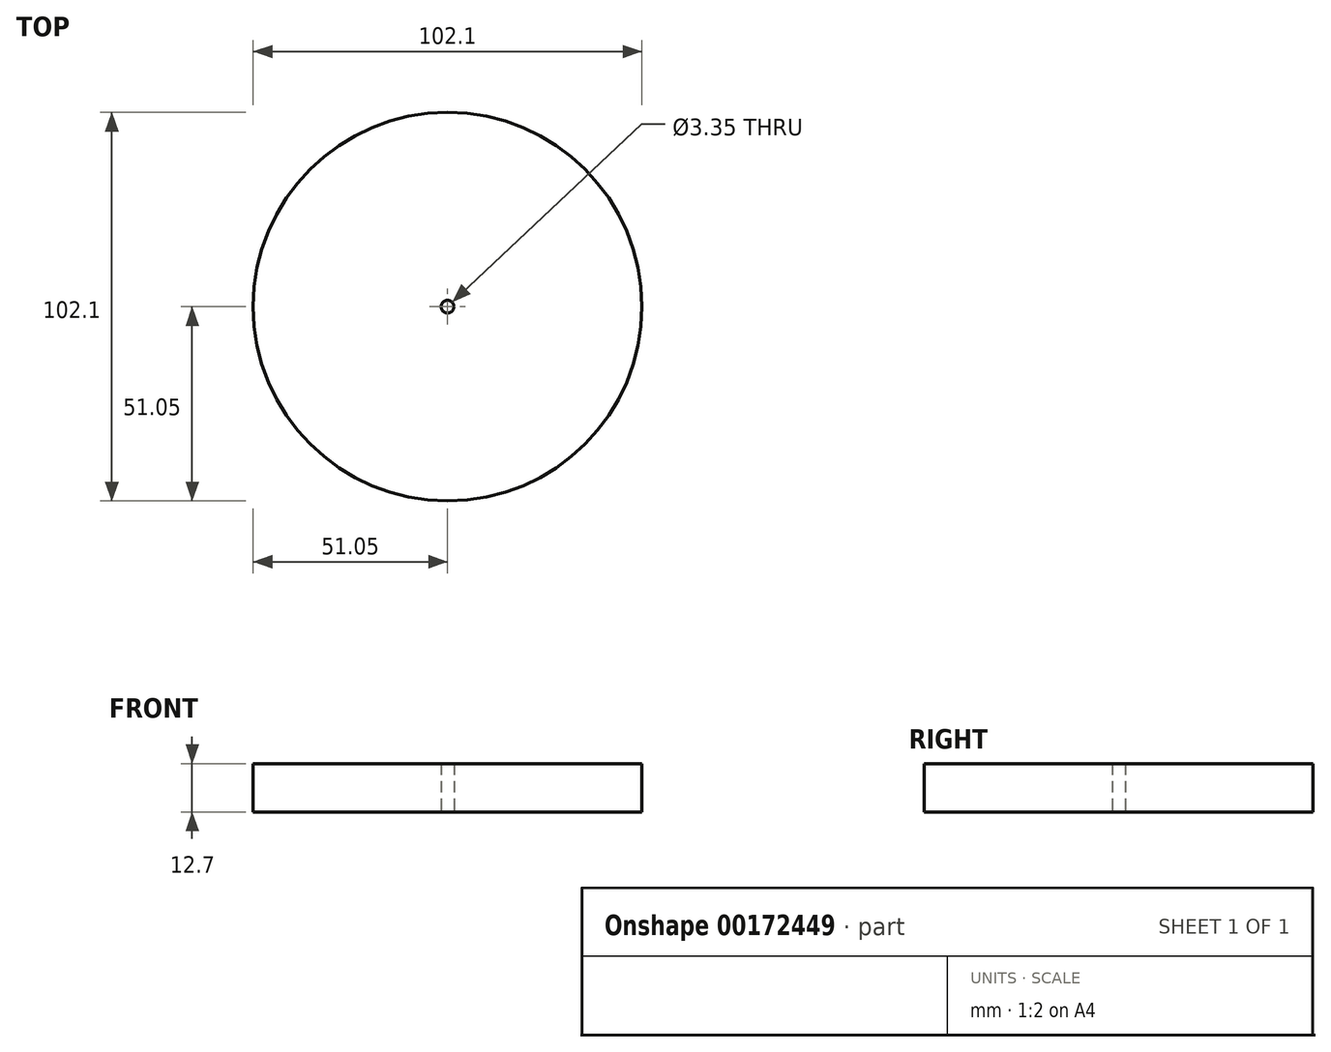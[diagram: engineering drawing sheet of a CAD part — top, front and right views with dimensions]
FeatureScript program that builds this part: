
annotation { "Feature Type Name" : "Feature", "Feature Type Description" : "" }
export const myFeature = defineFeature(function(context is Context, id is Id, definition is map)
    precondition{}
    {
        {
            var Q0;
            Q0=qCreatedBy(makeId("Top.planeOp"),FACE);
            var sketch = newSketch(context, id + "F0", { "sketchPlane" : qUnion([Q0])});
            skCircle(sketch, "E0", {"center": v(0, 0) * mm, "radius": 51.05 * mm});
            skCircle(sketch, "E1", {"center": v(0, 0) * mm, "radius": 22.35 * mm});
            skCircle(sketch, "E2", {"center": v(0, 0) * mm, "radius": 11.28 * mm});
            skCircle(sketch, "E3", {"center": v(0, 0) * mm, "radius": 8.6 * mm});
            skCircle(sketch, "E4", {"center": v(0, 0) * mm, "radius": 1.68 * mm});
            skSolve(sketch);
        }
        {
            var Q0;
            Q0=makeQuery(id+"F0.imprint","IMPRINT",FACE,{"disambiguationData":[TD([[makeQuery(id+"F0.imprint","IMPRINT",EDGE,{"derivedFrom":sQuery(id+"F0.wireOp",EDGE,"E0")}),1.0]])]});
            var Q1;
            Q1=makeQuery(id+"F0.imprint","IMPRINT",FACE,{"disambiguationData":[TD([[makeQuery(id+"F0.imprint","IMPRINT",EDGE,{"derivedFrom":sQuery(id+"F0.wireOp",EDGE,"E2")}),1.0]])]});
            var Q2;
            Q2=makeQuery(id+"F0.imprint","IMPRINT",FACE,{"disambiguationData":[TD([[makeQuery(id+"F0.imprint","IMPRINT",EDGE,{"derivedFrom":sQuery(id+"F0.wireOp",EDGE,"E3")}),1.0]])]});
            var Q3;
            Q3=makeQuery(id+"F0.imprint","IMPRINT",FACE,{"disambiguationData":[TD([[makeQuery(id+"F0.imprint","IMPRINT",EDGE,{"derivedFrom":sQuery(id+"F0.wireOp",EDGE,"E1")}),1.0]])]});
            extrude(context, id + "F1", {"entities" : qUnion([Q0, Q1, Q2, Q3]), "depth" : 12.7 * mm});
        }
    });
